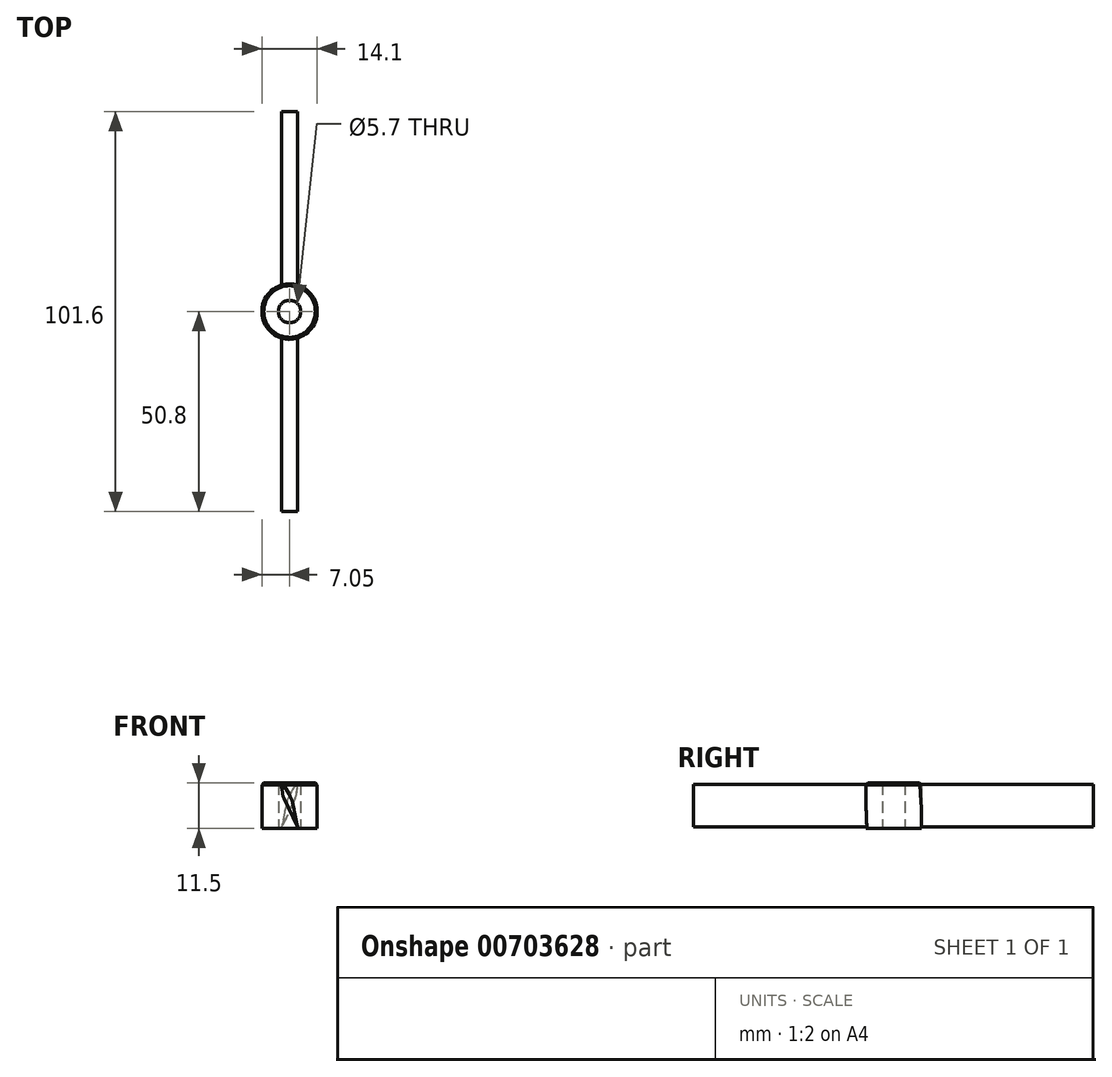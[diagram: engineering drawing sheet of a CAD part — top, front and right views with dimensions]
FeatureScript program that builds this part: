
annotation { "Feature Type Name" : "Feature", "Feature Type Description" : "" }
export const myFeature = defineFeature(function(context is Context, id is Id, definition is map)
    precondition{}
    {
        {
            var Q0;
            Q0=qCreatedBy(makeId("Top.planeOp"),FACE);
            var sketch = newSketch(context, id + "F0", { "sketchPlane" : qUnion([Q0])});
            skLineSegment(sketch, "E0", {"start": v(0, 0) * mm, "end": v(0, 50.8) * mm, "construction": true});
            skLineSegment(sketch, "E1", {"start": v(0, 0) * mm, "end": v(0, -50.8) * mm, "construction": true});
            skCircle(sketch, "E2", {"center": v(0, 0) * mm, "radius": 2.85 * mm});
            skCircle(sketch, "E3.0", {"center": v(0, 0) * mm, "radius": 7.05 * mm});
            skSolve(sketch);
        }
        {
            var Q0;
            Q0=makeQuery(id+"F0.imprint","IMPRINT",FACE,{"disambiguationData":[TD([[makeQuery(id+"F0.imprint","IMPRINT",EDGE,{"derivedFrom":sQuery(id+"F0.wireOp",EDGE,"E2")}),-1.0]])]});
            var Q1;
            Q1=makeQuery(id+"F0.imprint","IMPRINT",FACE,{"disambiguationData":[TD([[makeQuery(id+"F0.imprint","IMPRINT",EDGE,{"derivedFrom":sQuery(id+"F0.wireOp",EDGE,"E2")}),1.0]])]});
            extrude(context, id + "F1", {"entities" : qUnion([Q0, Q1]), "depth" : 11.5 * mm, "offsetDistance" : 25 * mm});
        }
        {
            var Q0;
            Q0=qCreatedBy(makeId("Front.planeOp"),FACE);
            var sketch = newSketch(context, id + "F2", { "sketchPlane" : qUnion([Q0])});
            skLineSegment(sketch, "E4", {"start": v(7.05, 6.9) * mm, "end": v(7.05, 0) * mm});
            skLineSegment(sketch, "E5", {"start": v(7.05, 0) * mm, "end": v(0, 0) * mm});
            skLineSegment(sketch, "E6", {"start": v(7.05, 4.07) * mm, "end": v(7.05, 0) * mm});
            skLineSegment(sketch, "E7", {"start": v(7.05, 3.95) * mm, "end": v(7.05, 5.45) * mm});
            skLineSegment(sketch, "E8", {"start": v(7.05, 4.95) * mm, "end": v(7.05, 3.75) * mm});
            skPoint(sketch, "E9.endSnap0", {"position": v(7.05, 2.04) * mm});
            skPoint(sketch, "E10", {"position": v(0, 5.75) * mm});
            skLineSegment(sketch, "E11", {"start": v(0, 0) * mm, "end": v(0, 11.5) * mm, "construction": true});
            skPoint(sketch, "E12", {"position": v(0.34, 3.8) * mm});
            skLineSegment(sketch, "E13.MirrorCS", {"start": v(-1.75, 8.33) * mm, "end": v(1.97, 0.33) * mm});
            skFitSpline(sketch, "E14.MirrorCS", {"points": [v(-1.75, 8.33) * mm, v(-1.97, 11.17) * mm, v(-0.26, 9.02) * mm, v(0.74, 6.53) * mm, v(1.36, 3.43) * mm, v(1.97, 0.33) * mm], "startDerivative": vector(-2.24, 21.88) * mm, "endDerivative": vector(3.05, -14.69) * mm});
            skLineSegment(sketch, "E15.MirrorCS", {"start": v(0.68, 3.11) * mm, "end": v(1.36, 3.43) * mm, "construction": true});
            skLineSegment(sketch, "E16.MirrorCS", {"start": v(-0.62, 5.9) * mm, "end": v(0.74, 6.53) * mm, "construction": true});
            skLineSegment(sketch, "E17.MirrorCS", {"start": v(-2.88, 10.75) * mm, "end": v(-1.97, 11.17) * mm, "construction": true});
            skLineSegment(sketch, "E18.MirrorCS", {"start": v(-1.75, 8.33) * mm, "end": v(-0.26, 9.02) * mm, "construction": true});
            skLineSegment(sketch, "E19.MirrorCS", {"start": v(-0.62, 5.9) * mm, "end": v(-2.88, 10.75) * mm, "construction": true});
            skLineSegment(sketch, "E20.MirrorCS", {"start": v(-0.62, 5.9) * mm, "end": v(1.97, 0.33) * mm, "construction": true});
            skLineSegment(sketch, "E21.MirrorCS", {"start": v(0, 5.75) * mm, "end": v(-0.47, 5.58) * mm, "construction": true});
            skLineSegment(sketch, "E22.MirrorCS", {"start": v(-1.97, 11.17) * mm, "end": v(1.97, 0.33) * mm, "construction": true});
            skLineSegment(sketch, "E23.MirrorCS", {"start": v(0, 5.75) * mm, "end": v(0.85, 6.06) * mm, "construction": true});
            skSolve(sketch);
        }
        {
            var Q0;
            Q0=makeQuery(id+"F2.imprint","IMPRINT",FACE,{"disambiguationData":[TD([[makeQuery(id+"F2.imprint","IMPRINT",EDGE,{"derivedFrom":sQuery(id+"F2.wireOp",EDGE,"E13.MirrorCS")}),1.0]])]});
            extrude(context, id + "F3", {"entities" : qUnion([Q0]), "operationType" : NewBodyOperationType.ADD, "depth" : 50.8 * mm, "offsetDistance" : 25 * mm});
        }
        {
            var Q0;
            {var subQ0=sQuery(id+"F2.wireOp",EDGE,"E13.MirrorCS");var subQ1=sQuery(id+"F2.wireOp",EDGE,"E14.MirrorCS");Q0=makeQuery(id+"F3.boolean.opBoolean","SPLIT",EDGE,{"disambiguationData":[TD([makeQuery(id+"F1.opExtrude","SWEPT_FACE",FACE,{"disambiguationData":[OSD([sQuery(id+"F0.wireOp",EDGE,"E3.0")])]})])],"derivedFrom":makeQuery(id+"F3.opExtrude","SWEPT_EDGE",EDGE,{"disambiguationData":[OSD([subQ0,subQ1]),TDD([makeQuery(id+"F2.imprint","INTERSECT",VERTEX,{"disambiguationData":[OD(0.0)],"derivedFrom":[subQ0,subQ1]})])]})});}
            fillet(context, id + "F4", {"entities" : qUnion([Q0]), "radius" : 5 * mm, "tangentPropagation" : true, "allowEdgeOverflow" : false});
        }
        {
            var Q0;
            Q0=qCreatedBy(makeId("Front.planeOp"),FACE);
            var sketch = newSketch(context, id + "F5", { "sketchPlane" : qUnion([Q0])});
            skLineSegment(sketch, "E24", {"start": v(7.05, 6.9) * mm, "end": v(7.05, 0) * mm});
            skLineSegment(sketch, "E25", {"start": v(7.05, 0) * mm, "end": v(0, 0) * mm});
            skLineSegment(sketch, "E26", {"start": v(7.05, 4.07) * mm, "end": v(7.05, 0) * mm});
            skLineSegment(sketch, "E27", {"start": v(7.05, 3.95) * mm, "end": v(7.05, 5.45) * mm});
            skLineSegment(sketch, "E28", {"start": v(7.05, 4.95) * mm, "end": v(7.05, 3.75) * mm});
            skPoint(sketch, "E29.endSnap0", {"position": v(7.05, 2.04) * mm});
            skPoint(sketch, "E30", {"position": v(0, 5.75) * mm});
            skPoint(sketch, "E31", {"position": v(-0.34, 3.8) * mm});
            skLineSegment(sketch, "E32", {"start": v(0, 0) * mm, "end": v(0, 11.5) * mm, "construction": true});
            skLineSegment(sketch, "E33.MirrorCS", {"start": v(1.75, 8.33) * mm, "end": v(-1.97, 0.33) * mm});
            skLineSegment(sketch, "E34.MirrorCS", {"start": v(0.62, 5.9) * mm, "end": v(-0.74, 6.53) * mm, "construction": true});
            skLineSegment(sketch, "E35.MirrorCS", {"start": v(1.75, 8.33) * mm, "end": v(0.26, 9.02) * mm, "construction": true});
            skLineSegment(sketch, "E36.MirrorCS", {"start": v(-0.68, 3.11) * mm, "end": v(-1.36, 3.43) * mm, "construction": true});
            skLineSegment(sketch, "E37.MirrorCS", {"start": v(0, 5.75) * mm, "end": v(-0.85, 6.06) * mm, "construction": true});
            skLineSegment(sketch, "E38.MirrorCS", {"start": v(0.62, 5.9) * mm, "end": v(2.88, 10.75) * mm, "construction": true});
            skLineSegment(sketch, "E39.MirrorCS", {"start": v(1.97, 11.17) * mm, "end": v(-1.97, 0.33) * mm, "construction": true});
            skFitSpline(sketch, "E40.MirrorCS", {"points": [v(1.75, 8.33) * mm, v(1.97, 11.17) * mm, v(0.26, 9.02) * mm, v(-0.74, 6.53) * mm, v(-1.36, 3.43) * mm, v(-1.97, 0.33) * mm], "startDerivative": vector(2.24, 21.88) * mm, "endDerivative": vector(-3.05, -14.69) * mm});
            skLineSegment(sketch, "E41.MirrorCS", {"start": v(0, 5.75) * mm, "end": v(0.47, 5.58) * mm, "construction": true});
            skLineSegment(sketch, "E42.MirrorCS", {"start": v(2.88, 10.75) * mm, "end": v(1.97, 11.17) * mm, "construction": true});
            skLineSegment(sketch, "E43.MirrorCS", {"start": v(0.62, 5.9) * mm, "end": v(-1.97, 0.33) * mm, "construction": true});
            skSolve(sketch);
        }
        {
            var Q0;
            Q0=makeQuery(id+"F5.imprint","IMPRINT",FACE,{"disambiguationData":[TD([[makeQuery(id+"F5.imprint","IMPRINT",EDGE,{"derivedFrom":sQuery(id+"F5.wireOp",EDGE,"E33.MirrorCS")}),-1.0]])]});
            extrude(context, id + "F6", {"entities" : qUnion([Q0]), "operationType" : NewBodyOperationType.ADD, "oppositeDirection" : true, "depth" : 50.8 * mm, "offsetDistance" : 25 * mm});
        }
        {
            var Q0;
            {var subQ0=sQuery(id+"Fv6gQINzxOytYec_1.wireOp",EDGE,"d878019e-00ca-4c95-9281-a5dbebea3d630.MirrorCS");var subQ1=sQuery(id+"Fv6gQINzxOytYec_1.wireOp",EDGE,"19222e45-0a99-4dbb-b0f8-06b7d0d080b00.MirrorCS");Q0=makeQuery(id+"F6.opExtrude","SWEPT_EDGE",EDGE,{"disambiguationData":[OSD([subQ1,subQ0]),TDD([makeQuery(id+"Fv6gQINzxOytYec_1.imprint","INTERSECT",VERTEX,{"disambiguationData":[OD(0.0)],"derivedFrom":[subQ1,subQ0]})])]});}
            var Q1;
            {var subQ0=sQuery(id+"Fj0TBoSZPlOelra_1.wireOp",EDGE,"c5e6d0e3-df62-49b4-9d73-401119eaf40d2.MirrorCS");var subQ1=sQuery(id+"Fj0TBoSZPlOelra_1.wireOp",EDGE,"c5e6d0e3-df62-49b4-9d73-401119eaf40d1.MirrorCS");Q1=makeQuery(id+"F6.opExtrude","SWEPT_EDGE",EDGE,{"disambiguationData":[OSD([subQ1,subQ0]),TDD([makeQuery(id+"Fj0TBoSZPlOelra_1.imprint","INTERSECT",VERTEX,{"disambiguationData":[OD(0.0)],"derivedFrom":[subQ1,subQ0]})])]});}
            var Q2;
            {var subQ0=sQuery(id+"F5.wireOp",EDGE,"f684c9b4-9527-4a63-8f31-0619753b8ec57.MirrorCS");var subQ1=sQuery(id+"F5.wireOp",EDGE,"f684c9b4-9527-4a63-8f31-0619753b8ec52.MirrorCS");Q2=makeQuery(id+"F6.opExtrude","SWEPT_EDGE",EDGE,{"disambiguationData":[OSD([subQ1,subQ0]),TDD([makeQuery(id+"F5.imprint","INTERSECT",VERTEX,{"disambiguationData":[OD(0.0)],"derivedFrom":[subQ1,subQ0]})])]});}
            var Q3;
            {var subQ0=sQuery(id+"F5.wireOp",EDGE,"E33.MirrorCS");var subQ1=sQuery(id+"F5.wireOp",EDGE,"E40.MirrorCS");Q3=makeQuery(id+"F6.boolean.opBoolean","SPLIT",EDGE,{"disambiguationData":[TD([makeQuery(id+"F1.opExtrude","SWEPT_FACE",FACE,{"disambiguationData":[OSD([sQuery(id+"F0.wireOp",EDGE,"E3.0")])]})])],"derivedFrom":makeQuery(id+"F6.opExtrude","SWEPT_EDGE",EDGE,{"disambiguationData":[OSD([subQ0,subQ1]),TDD([makeQuery(id+"F5.imprint","INTERSECT",VERTEX,{"disambiguationData":[OD(0.0)],"derivedFrom":[subQ0,subQ1]})])]})});}
            fillet(context, id + "F7", {"entities" : qUnion([Q0, Q1, Q2, Q3]), "radius" : 5 * mm, "tangentPropagation" : true, "allowEdgeOverflow" : false});
        }
        {
            var Q0;
            Q0=makeQuery(id+"F1.opExtrude","CAP_EDGE",EDGE,{"disambiguationData":[OSD([sQuery(id+"F0.wireOp",EDGE,"E3.0")])],"isStart":false});
            chamfer(context, id + "F8", {"entities" : qUnion([Q0]), "width" : .5 * mm, "tangentPropagation" : true});
        }
        {
            var Q0;
            Q0=makeQuery(id+"F0.imprint","IMPRINT",FACE,{"disambiguationData":[TD([[makeQuery(id+"F0.imprint","IMPRINT",EDGE,{"derivedFrom":sQuery(id+"F0.wireOp",EDGE,"E2")}),1.0]])]});
            extrude(context, id + "F9", {"entities" : qUnion([Q0]), "operationType" : NewBodyOperationType.REMOVE, "depth" : 25 * mm, "offsetDistance" : 25 * mm});
        }
    });
